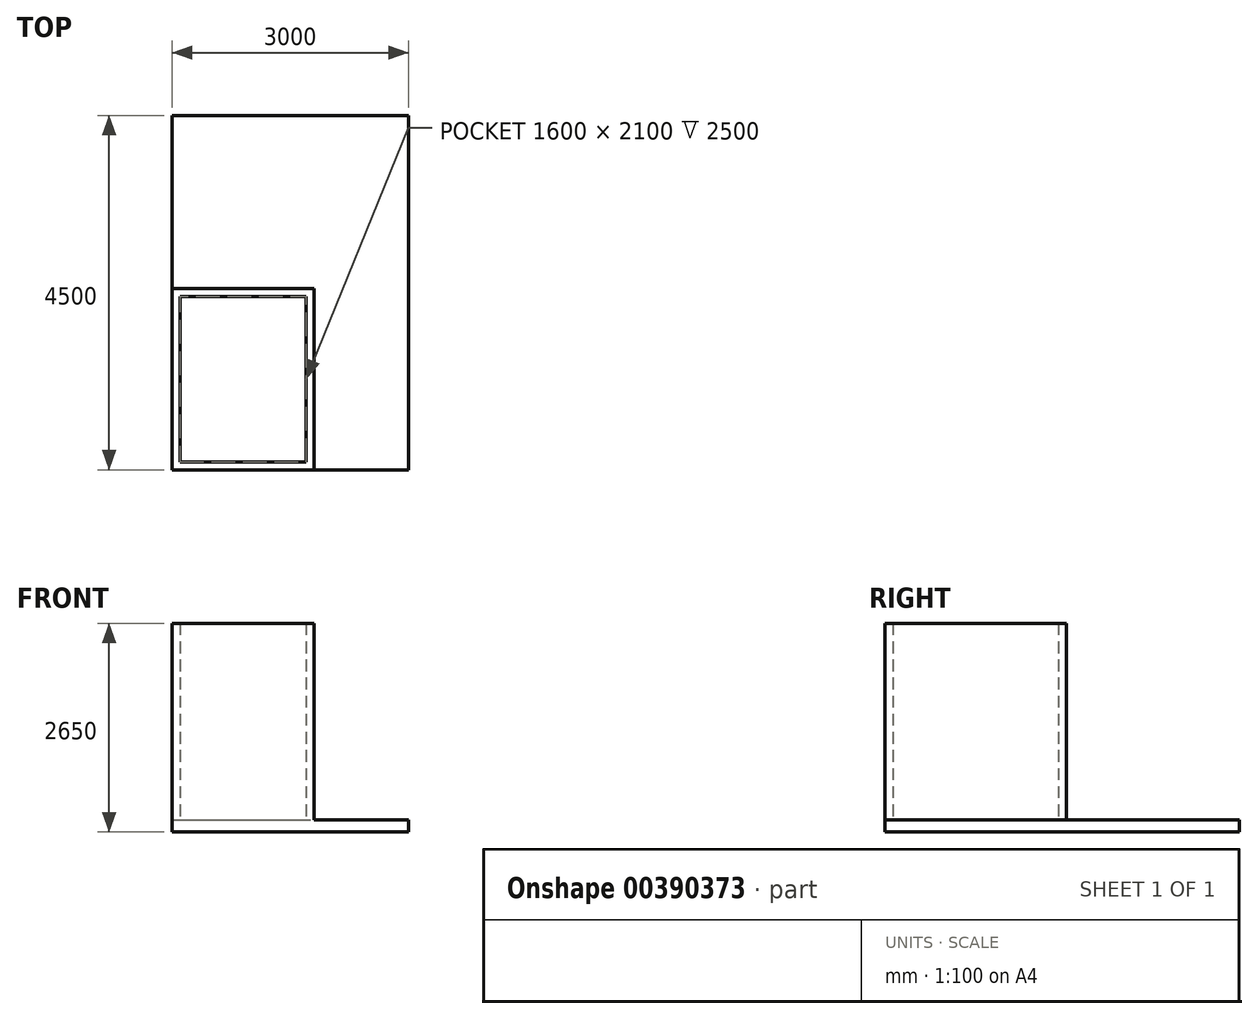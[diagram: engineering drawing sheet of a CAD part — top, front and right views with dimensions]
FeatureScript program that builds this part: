
annotation { "Feature Type Name" : "Feature", "Feature Type Description" : "" }
export const myFeature = defineFeature(function(context is Context, id is Id, definition is map)
    precondition{}
    {
        {
            var Q0;
            Q0=qCreatedBy(makeId("Top.planeOp"),FACE);
            var sketch = newSketch(context, id + "F0", { "sketchPlane" : qUnion([Q0])});
            skLineSegment(sketch, "E0.bottom", {"start": v(-1500, 2250) * mm, "end": v(1500, 2250) * mm});
            skLineSegment(sketch, "E0.top", {"start": v(-1500, -2250) * mm, "end": v(1500, -2250) * mm});
            skLineSegment(sketch, "E0.left", {"start": v(-1500, 2250) * mm, "end": v(-1500, -2250) * mm});
            skLineSegment(sketch, "E0.right", {"start": v(1500, 2250) * mm, "end": v(1500, -2250) * mm});
            skPoint(sketch, "E0.middle", {"position": v(0, 0) * mm});
            skSolve(sketch);
        }
        {
            var Q0;
            Q0=makeQuery(id+"F0.imprint","IMPRINT",FACE,{"disambiguationData":[TD([[makeQuery(id+"F0.imprint","IMPRINT",EDGE,{"derivedFrom":sQuery(id+"F0.wireOp",EDGE,"E0.bottom")}),-1.0]])]});
            extrude(context, id + "F1", {"entities" : qUnion([Q0]), "depth" : 150 * mm});
        }
        {
            var Q0;
            Q0=makeQuery(id+"F1.opExtrude","CAP_FACE",FACE,{"disambiguationData":[OSD([sQuery(id+"F0.wireOp",EDGE,"E0.bottom"),sQuery(id+"F0.wireOp",EDGE,"E0.top"),sQuery(id+"F0.wireOp",EDGE,"E0.left"),sQuery(id+"F0.wireOp",EDGE,"E0.right")])],"isStart":false});
            var sketch = newSketch(context, id + "F2", { "sketchPlane" : qUnion([Q0])});
            skLineSegment(sketch, "E1.bottom", {"start": v(-1500, -2250) * mm, "end": v(300, -2250) * mm});
            skLineSegment(sketch, "E1.top", {"start": v(-1500, 50) * mm, "end": v(300, 50) * mm});
            skLineSegment(sketch, "E1.left", {"start": v(-1500, -2250) * mm, "end": v(-1500, 50) * mm});
            skLineSegment(sketch, "E1.right", {"start": v(300, -2250) * mm, "end": v(300, 50) * mm});
            skLineSegment(sketch, "E2.0", {"start": v(-1400, -50) * mm, "end": v(200, -50) * mm});
            skLineSegment(sketch, "E2.1", {"start": v(-1400, -2150) * mm, "end": v(-1400, -50) * mm});
            skLineSegment(sketch, "E2.2", {"start": v(-1400, -2150) * mm, "end": v(200, -2150) * mm});
            skLineSegment(sketch, "E2.3", {"start": v(200, -2150) * mm, "end": v(200, -50) * mm});
            skSolve(sketch);
        }
        {
            var Q0;
            {var subQ4=sQuery(id+"F2.wireOp",EDGE,"E1.top");Q0=makeQuery(id+"F2.imprint","IMPRINT",FACE,{"disambiguationData":[TD([[makeQuery(id+"F2.imprint","IMPRINT",EDGE,{"derivedFrom":subQ4}),1.0]])]});}
            var sketch = newSketch(context, id + "F3", { "sketchPlane" : qUnion([Q0])});
            skLineSegment(sketch, "E3", {"start": v(-1620.37, 750) * mm, "end": v(1684.53, 750) * mm});
            skSolve(sketch);
        }
        {
            var Q0;
            Q0=makeQuery(id+"F2.imprint","IMPRINT",FACE,{"disambiguationData":[TD([[makeQuery(id+"F2.imprint","IMPRINT",EDGE,{"derivedFrom":sQuery(id+"F2.wireOp",EDGE,"E1.bottom")}),1.0]])]});
            extrude(context, id + "F4", {"entities" : qUnion([Q0]), "operationType" : NewBodyOperationType.ADD, "depth" : 2500 * mm});
        }
        {
            var Q0;
            Q0=makeQuery(id+"F4.boolean.opBoolean","MERGE",FACE,{"derivedFrom":[makeQuery(id+"F1.opExtrude","SWEPT_FACE",FACE,{"disambiguationData":[OSD([sQuery(id+"F0.wireOp",EDGE,"E0.top")])]}),makeQuery(id+"F4.opExtrude","SWEPT_FACE",FACE,{"disambiguationData":[OSD([sQuery(id+"F2.wireOp",EDGE,"E1.bottom")])]})]});
            var sketch = newSketch(context, id + "F5", { "sketchPlane" : qUnion([Q0])});
            skLineSegment(sketch, "E4", {"start": v(-1500, 2650) * mm, "end": v(300, 2332.61) * mm});
            skLineSegment(sketch, "E5", {"start": v(300, 2332.61) * mm, "end": v(300, 2650) * mm});
            skLineSegment(sketch, "E6", {"start": v(300, 2650) * mm, "end": v(-1500, 2650) * mm});
            skSolve(sketch);
        }
        {
            var Q0;
            Q0=makeQuery(id+"F5.imprint","IMPRINT",FACE,{"disambiguationData":[TD([[makeQuery(id+"F5.imprint","IMPRINT",EDGE,{"derivedFrom":sQuery(id+"F5.wireOp",EDGE,"E4")}),1.0]])]});
            var Q1;
            Q1=makeQuery(id+"F4.opExtrude","SWEPT_FACE",FACE,{"disambiguationData":[OSD([sQuery(id+"F2.wireOp",EDGE,"E1.top")])]});
            extrude(context, id + "F6", {"entities" : qUnion([Q0]), "operationType" : NewBodyOperationType.REMOVE, "endBound" : BoundingType.UP_TO_SURFACE, "oppositeDirection" : true, "endBoundEntityFace" : qUnion([Q1]), "depth" : 25 * mm});
        }
        {
            var Q0;
            Q0=makeQuery(id+"F4.boolean.opBoolean","MERGE",FACE,{"derivedFrom":[makeQuery(id+"F1.opExtrude","SWEPT_FACE",FACE,{"disambiguationData":[OSD([sQuery(id+"F0.wireOp",EDGE,"E0.top")])]}),makeQuery(id+"F4.opExtrude","SWEPT_FACE",FACE,{"disambiguationData":[OSD([sQuery(id+"F2.wireOp",EDGE,"E1.bottom")])]})]});
            var sketch = newSketch(context, id + "F7", { "sketchPlane" : qUnion([Q0])});
            skLineSegment(sketch, "E7.bottom", {"start": v(-1285, 2250) * mm, "end": v(-385, 2250) * mm});
            skLineSegment(sketch, "E7.top", {"start": v(-1285, 150) * mm, "end": v(-385, 150) * mm});
            skLineSegment(sketch, "E7.left", {"start": v(-1285, 2250) * mm, "end": v(-1285, 150) * mm});
            skLineSegment(sketch, "E7.right", {"start": v(-385, 2250) * mm, "end": v(-385, 150) * mm});
            skSolve(sketch);
        }
        {
            var Q0;
            Q0 = qSketchRegion(id + "F7", true);
            extrude(context, id + "F8", {"entities" : qUnion([Q0]), "operationType" : NewBodyOperationType.REMOVE, "oppositeDirection" : true, "depth" : 800 * mm});
        }
        {
            var Q0;
            Q0=makeQuery(id+"F4.opExtrude","SWEPT_FACE",FACE,{"disambiguationData":[OSD([sQuery(id+"F2.wireOp",EDGE,"E1.top")])]});
            var sketch = newSketch(context, id + "F9", { "sketchPlane" : qUnion([Q0])});
            skLineSegment(sketch, "E8.bottom", {"start": v(100, 150) * mm, "end": v(-200, 150) * mm});
            skLineSegment(sketch, "E8.top", {"start": v(100, 650) * mm, "end": v(-200, 650) * mm});
            skLineSegment(sketch, "E8.left", {"start": v(100, 150) * mm, "end": v(100, 650) * mm});
            skLineSegment(sketch, "E8.right", {"start": v(-200, 150) * mm, "end": v(-200, 650) * mm});
            skSolve(sketch);
        }
        {
            var Q0;
            Q0=makeQuery(id+"F9.imprint","IMPRINT",FACE,{"disambiguationData":[TD([[makeQuery(id+"F9.imprint","IMPRINT",EDGE,{"derivedFrom":sQuery(id+"F9.wireOp",EDGE,"E8.bottom")}),-1.0]])]});
            extrude(context, id + "F10", {"entities" : qUnion([Q0]), "operationType" : NewBodyOperationType.REMOVE, "endBound" : BoundingType.UP_TO_NEXT, "oppositeDirection" : true, "depth" : 25 * mm});
        }
        {
            var Q0;
            Q0=makeQuery(id+"F2.imprint","IMPRINT",FACE,{"disambiguationData":[TD([[makeQuery(id+"F2.imprint","IMPRINT",EDGE,{"derivedFrom":sQuery(id+"F2.wireOp",EDGE,"E1.bottom")}),1.0]])]});
            extrude(context, id + "F11", {"entities" : qUnion([Q0]), "operationType" : NewBodyOperationType.ADD, "depth" : 2500 * mm});
        }
    });
